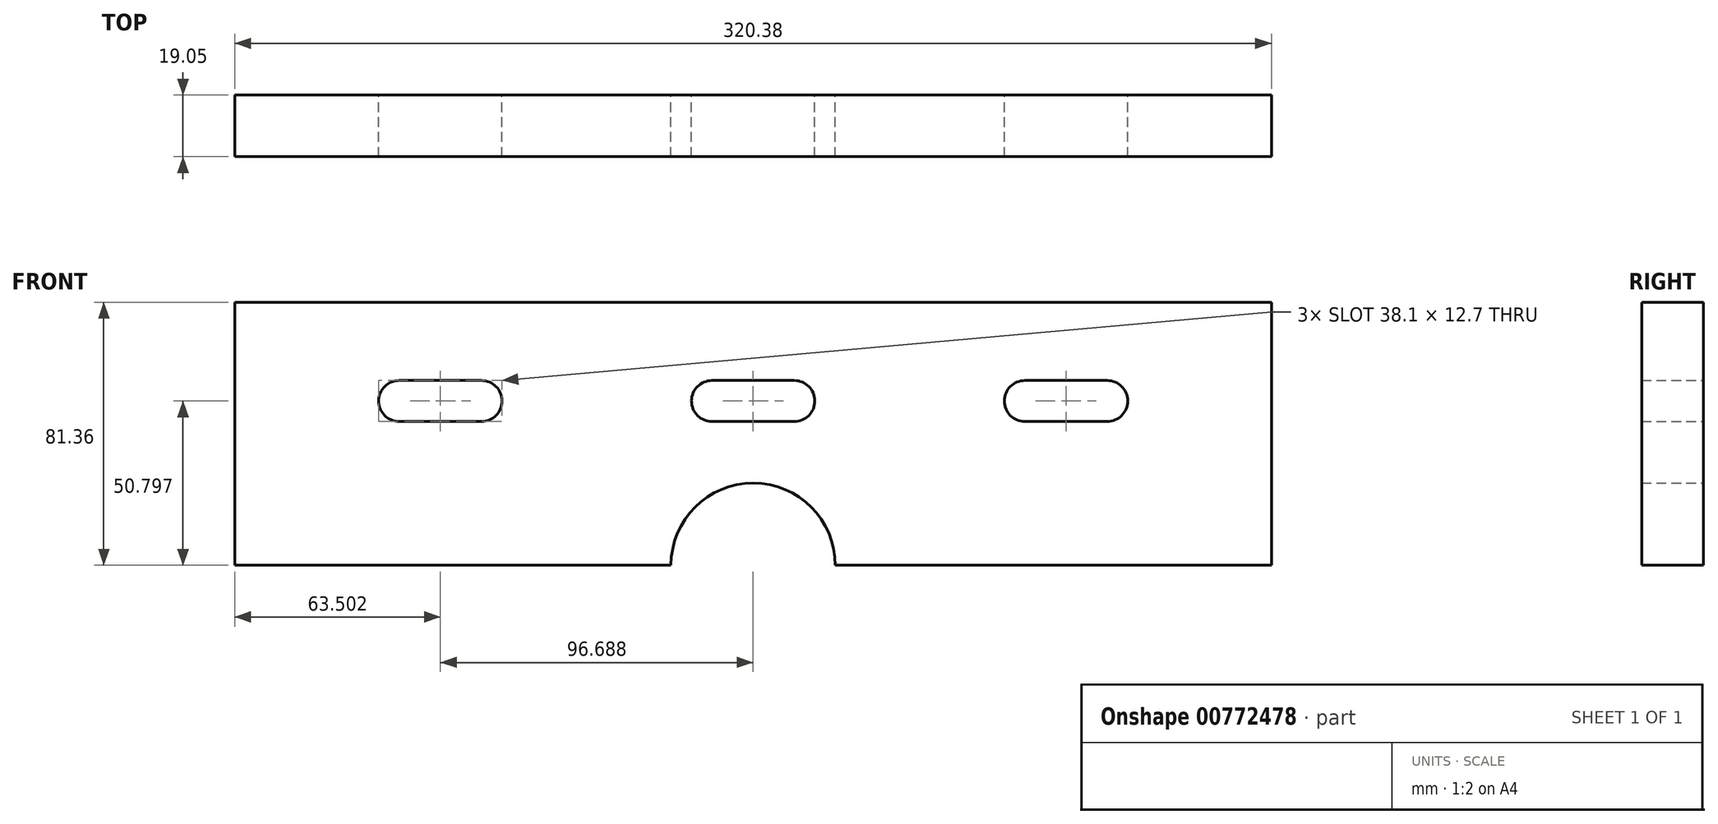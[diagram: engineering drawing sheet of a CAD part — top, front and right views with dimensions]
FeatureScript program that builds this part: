
annotation { "Feature Type Name" : "Feature", "Feature Type Description" : "" }
export const myFeature = defineFeature(function(context is Context, id is Id, definition is map)
    precondition{}
    {
        {
            var Q0;
            Q0=qCreatedBy(makeId("Front.planeOp"),FACE);
            var sketch = newSketch(context, id + "F0", { "sketchPlane" : qUnion([Q0])});
            skLineSegment(sketch, "E0", {"start": v(-25.4, -40.68) * mm, "end": v(-160.19, -40.68) * mm});
            skLineSegment(sketch, "E1", {"start": v(-160.19, -40.68) * mm, "end": v(-160.19, 40.68) * mm});
            skLineSegment(sketch, "E2", {"start": v(-160.19, 40.68) * mm, "end": v(160.19, 40.68) * mm});
            skLineSegment(sketch, "E3", {"start": v(160.19, 40.68) * mm, "end": v(160.19, -40.68) * mm});
            skLineSegment(sketch, "E4", {"start": v(160.19, -40.68) * mm, "end": v(25.4, -40.68) * mm});
            skArc(sketch, "E5", {"start": v(-109.39, 16.47) * mm, "mid": v(-115.74, 10.12) * mm, "end": v(-109.39, 3.77) * mm});
            skArc(sketch, "E6", {"start": v(-83.99, 3.77) * mm, "mid": v(-77.64, 10.12) * mm, "end": v(-83.99, 16.47) * mm});
            skLineSegment(sketch, "E7", {"start": v(-109.39, 16.47) * mm, "end": v(-83.99, 16.47) * mm});
            skLineSegment(sketch, "E8", {"start": v(-109.39, 3.77) * mm, "end": v(-83.99, 3.77) * mm});
            skArc(sketch, "E9", {"start": v(109.39, 3.77) * mm, "mid": v(115.74, 10.12) * mm, "end": v(109.39, 16.47) * mm});
            skArc(sketch, "E10", {"start": v(83.99, 16.47) * mm, "mid": v(77.64, 10.12) * mm, "end": v(83.99, 3.77) * mm});
            skLineSegment(sketch, "E11", {"start": v(109.39, 16.47) * mm, "end": v(83.99, 16.47) * mm});
            skLineSegment(sketch, "E12", {"start": v(109.39, 3.77) * mm, "end": v(83.99, 3.77) * mm});
            skArc(sketch, "E13", {"start": v(-12.7, 16.47) * mm, "mid": v(-19.05, 10.12) * mm, "end": v(-12.7, 3.77) * mm});
            skArc(sketch, "E14", {"start": v(12.7, 3.77) * mm, "mid": v(19.05, 10.12) * mm, "end": v(12.7, 16.47) * mm});
            skLineSegment(sketch, "E15", {"start": v(-12.7, 16.47) * mm, "end": v(12.7, 16.47) * mm});
            skLineSegment(sketch, "E16", {"start": v(-12.7, 3.77) * mm, "end": v(12.7, 3.77) * mm});
            skArc(sketch, "E17", {"start": v(25.4, -40.68) * mm, "mid": v(0, -15.28) * mm, "end": v(-25.4, -40.68) * mm});
            skSolve(sketch);
        }
        {
            var Q0;
            Q0=makeQuery(id+"F0.imprint","IMPRINT",FACE,{"disambiguationData":[TD([[makeQuery(id+"F0.imprint","IMPRINT",EDGE,{"derivedFrom":sQuery(id+"F0.wireOp",EDGE,"E0")}),-1.0]])]});
            extrude(context, id + "F1", {"entities" : qUnion([Q0]), "depth" : 19.05 * mm, "offsetDistance" : 25.4 * mm});
        }
    });
